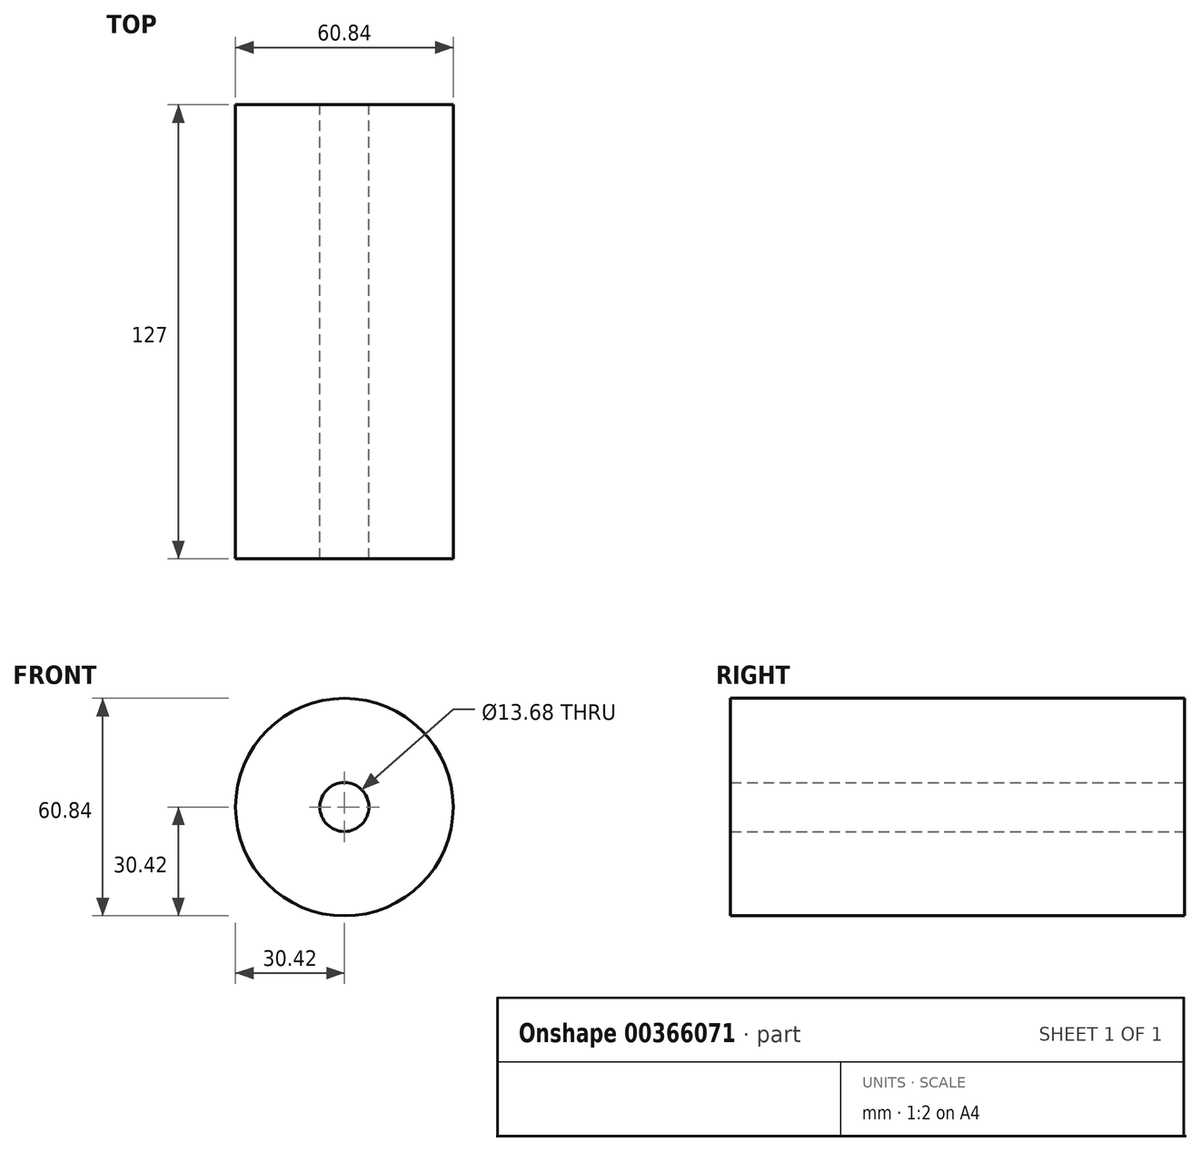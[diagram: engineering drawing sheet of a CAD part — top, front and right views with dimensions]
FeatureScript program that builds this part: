
annotation { "Feature Type Name" : "Feature", "Feature Type Description" : "" }
export const myFeature = defineFeature(function(context is Context, id is Id, definition is map)
    precondition{}
    {
        {
            var Q0;
            Q0=qCreatedBy(makeId("Front.planeOp"),FACE);
            var sketch = newSketch(context, id + "F0", { "sketchPlane" : qUnion([Q0])});
            skCircle(sketch, "E0", {"center": v(0, 0) * mm, "radius": 30.42 * mm});
            skSolve(sketch);
        }
        {
            var Q0;
            Q0 = qSketchRegion(id + "F0", true);
            extrude(context, id + "F1", {"entities" : qUnion([Q0]), "depth" : 127 * mm});
        }
        {
            var Q0;
            Q0=qCreatedBy(makeId("Front.planeOp"),FACE);
            var sketch = newSketch(context, id + "F2", { "sketchPlane" : qUnion([Q0])});
            skCircle(sketch, "E1", {"center": v(0, 0) * mm, "radius": 6.84 * mm});
            skSolve(sketch);
        }
        {
            var Q0;
            Q0=makeQuery(id+"F2.imprint","IMPRINT",FACE,{"disambiguationData":[TD([[makeQuery(id+"F2.imprint","IMPRINT",EDGE,{"derivedFrom":sQuery(id+"F2.wireOp",EDGE,"E1")}),1.0]])]});
            extrude(context, id + "F3", {"entities" : qUnion([Q0]), "operationType" : NewBodyOperationType.REMOVE, "depth" : 127 * mm});
        }
    });
